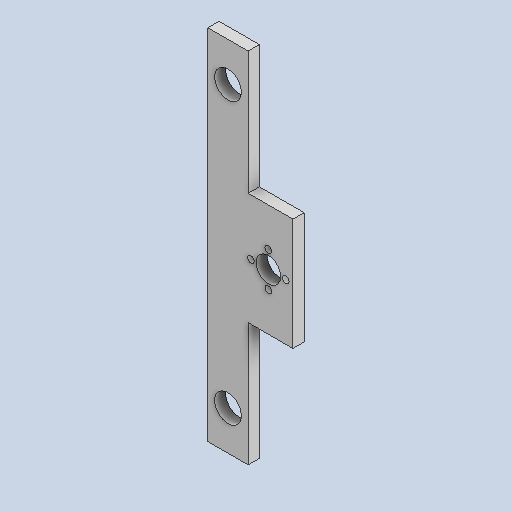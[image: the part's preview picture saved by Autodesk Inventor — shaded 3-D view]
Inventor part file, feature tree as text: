
AUTODESK INVENTOR PART (.ipt)
format: ipt  version: 2023.2 (Build 272271000, 271)  size: 414,720 bytes
history: native  units: mm
features: reference x4, other x3, sketch x2, extrude x1, hole x1
ambient origin geometry x8: Origin, YZ Plane, XZ Plane, XY Plane, X Axis, Y Axis, Z Axis, Center Point
bodies: Solid1 (feature_tree)
feature tree (11):
  extrude  "Extrusion1"  TaperAngle=90.0deg  [1 undecoded]
  hole  "Hole1"  [1 undecoded]
  sketch  "Sketch1"  dims[d0=160.0mm d1=90.0deg]
  sketch  "Sketch2"  dims[d2=18.0mm d3=12.0mm d4=12.0mm d5=125.113mm d6=20.0mm d7=50.0mm d8=55.0mm d11=5.0mm d12=0.0mm d15=11.0mm d16=9.0mm d17=17.4435mm d18=3.0mm d19=6.0mm d20=4.0mm d21=2.0mm d22=90.0deg d23=8.0mm d24=20.594885mm d25=9.0mm]
  reference  "Reference1"
  reference  "Reference2"
  reference  "Reference3"
  reference  "Reference4"
  parser-record x1  (decoder bookkeeping rows leaked as tree rows — omitted from the tree; the rows remain in map.json)
  other  "Main Assembly.iam"
  other  "ACME Brass Nut:1"
note: 2 required parameter values undecoded (feature->parameter linkage not recoverable at this tier; creation-order binding heuristic only, values carry confidence <= 0.55)
note: 1 file-system path scrubbed to <path> (originals preserved in map.json)
